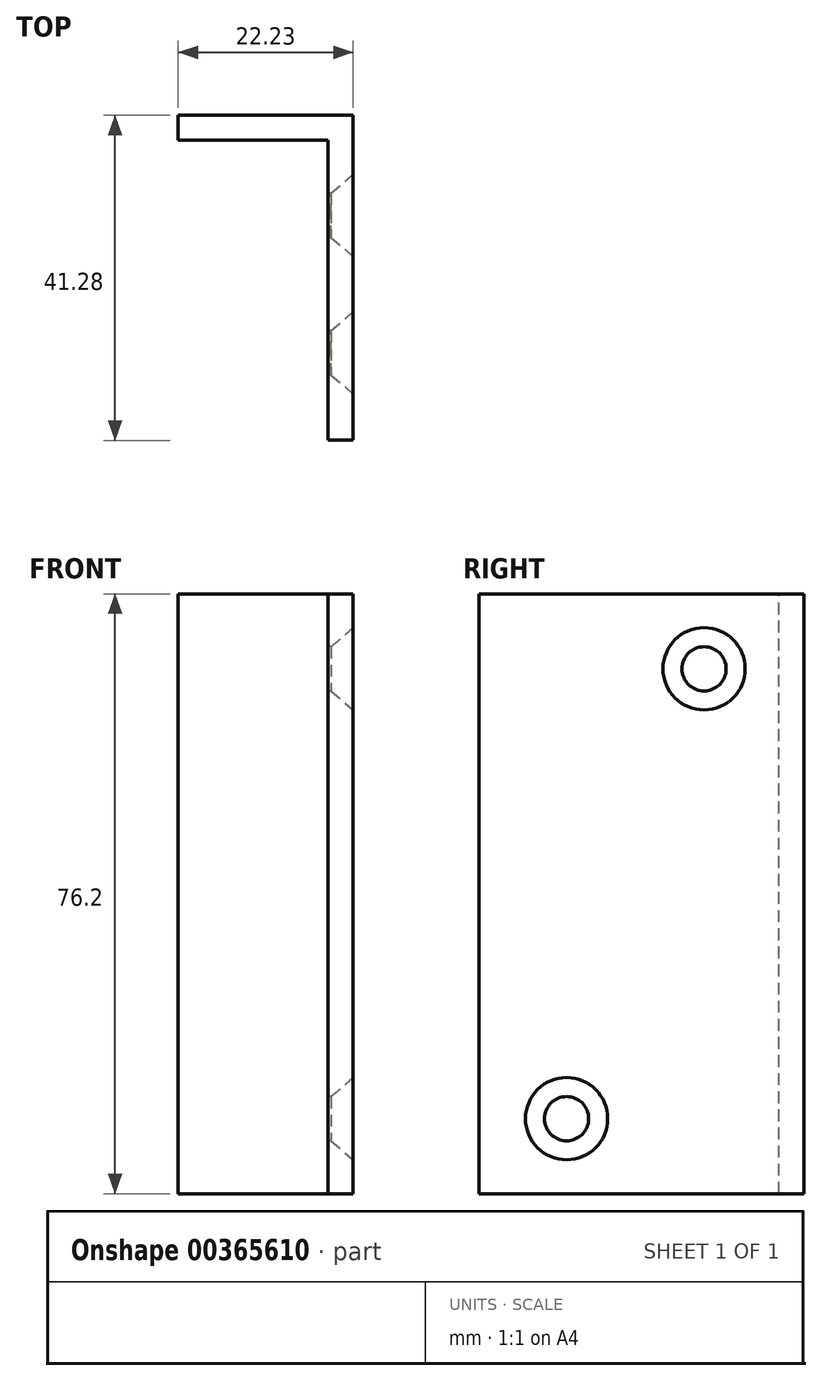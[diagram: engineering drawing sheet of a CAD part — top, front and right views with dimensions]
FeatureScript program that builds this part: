
annotation { "Feature Type Name" : "Feature", "Feature Type Description" : "" }
export const myFeature = defineFeature(function(context is Context, id is Id, definition is map)
    precondition{}
    {
        {
            var Q0;
            Q0=qCreatedBy(makeId("Right.planeOp"),FACE);
            var sketch = newSketch(context, id + "F0", { "sketchPlane" : qUnion([Q0])});
            skLineSegment(sketch, "E0.bottom", {"start": v(20.64, -38.1) * mm, "end": v(-20.64, -38.1) * mm});
            skLineSegment(sketch, "E0.top", {"start": v(20.64, 38.1) * mm, "end": v(-20.64, 38.1) * mm});
            skLineSegment(sketch, "E0.left", {"start": v(20.64, -38.1) * mm, "end": v(20.64, 38.1) * mm});
            skLineSegment(sketch, "E0.right", {"start": v(-20.64, -38.1) * mm, "end": v(-20.64, 38.1) * mm});
            skPoint(sketch, "E0.middle", {"position": v(0, 0) * mm});
            skSolve(sketch);
        }
        {
            var Q0;
            Q0=qSketchRegion(id+"F0",true);
            extrude(context, id + "F1", {"entities" : qUnion([Q0]), "depth" : 22.22 * mm, "offsetDistance" : 25.4 * mm});
        }
        {
            var Q0;
            Q0=makeQuery(id+"F1.opExtrude","CAP_FACE",FACE,{"disambiguationData":[OSD([sQuery(id+"F0.wireOp",EDGE,"E0.bottom"),sQuery(id+"F0.wireOp",EDGE,"E0.top"),sQuery(id+"F0.wireOp",EDGE,"E0.left"),sQuery(id+"F0.wireOp",EDGE,"E0.right")])],"isStart":false});
            var sketch = newSketch(context, id + "F2", { "sketchPlane" : qUnion([Q0])});
            skPoint(sketch, "E1", {"position": v(7.94, 28.58) * mm});
            skPoint(sketch, "E2", {"position": v(-9.53, -28.58) * mm});
            skSolve(sketch);
        }
        {
            var Q0;
            Q0=sQuery(id+"F2.wireOp",VERTEX,"9c0d3f73-d5ec-4d0f-aece-a9a309c8c5a9");
            var Q1;
            Q1=sQuery(id+"F2.wireOp",VERTEX,"E1");
            var Q2;
            Q2=sQuery(id+"F2.wireOp",VERTEX,"f748485d-7854-4512-8540-e9efd3eabb61");
            var Q3;
            Q3=sQuery(id+"F2.wireOp",VERTEX,"E2");
            var Q4;
            Q4=makeQuery(id+"F1.opExtrude","SWEPT_BODY",BODY,{"disambiguationData":[OSD([sQuery(id+"F0.wireOp",EDGE,"E0.bottom"),sQuery(id+"F0.wireOp",EDGE,"E0.top"),sQuery(id+"F0.wireOp",EDGE,"E0.left"),sQuery(id+"F0.wireOp",EDGE,"E0.right")])]});
            hole(context, id + "F3", {"style" : HoleStyle.C_SINK, "endStyle" : HoleEndStyle.THROUGH, "standardTappedOrClearance" : lookupTablePath({ "fit" : "Normal (ASME)", "standard" : "ANSI", "size" : "#10", "type" : "Clearance" }), "standardBlindInLast" : lookupTablePath({ "fit" : "Normal", "standard" : "ANSI", "engagement" : "75%", "pitch" : "24 tpi", "size" : "#10", "type" : "Clearance & tapped" }), "holeDiameter" : 5.61 * mm, "cSinkDiameter" : 10.44 * mm, "cSinkAngle" : 82 * degree, "majorDiameter" : 6.35 * mm, "isTappedThrough" : true, "tappedDepth" : 12.7 * mm, "tapClearance" : 3, "locations" : qUnion([Q0, Q1, Q2, Q3]), "scope" : qUnion([Q4]), "startStyle" : HoleStartStyle.SKETCH});
        }
        {
            var Q0;
            Q0=makeQuery(id+"F1.opExtrude","SWEPT_FACE",FACE,{"disambiguationData":[OSD([sQuery(id+"F0.wireOp",EDGE,"E0.top")])]});
            var sketch = newSketch(context, id + "F4", { "sketchPlane" : qUnion([Q0])});
            skLineSegment(sketch, "E3.bottom", {"start": v(0, -20.64) * mm, "end": v(19.05, -20.64) * mm});
            skLineSegment(sketch, "E3.top", {"start": v(0, 17.46) * mm, "end": v(19.05, 17.46) * mm});
            skLineSegment(sketch, "E3.left", {"start": v(0, -20.64) * mm, "end": v(0, 17.46) * mm});
            skLineSegment(sketch, "E3.right", {"start": v(19.05, -20.64) * mm, "end": v(19.05, 17.46) * mm});
            skSolve(sketch);
        }
        {
            var Q0;
            Q0 = qSketchRegion(id + "F4", true);
            extrude(context, id + "F5", {"entities" : qUnion([Q0]), "operationType" : NewBodyOperationType.REMOVE, "endBound" : BoundingType.THROUGH_ALL, "oppositeDirection" : true, "depth" : 25.4 * mm, "offsetDistance" : 25.4 * mm});
        }
    });
